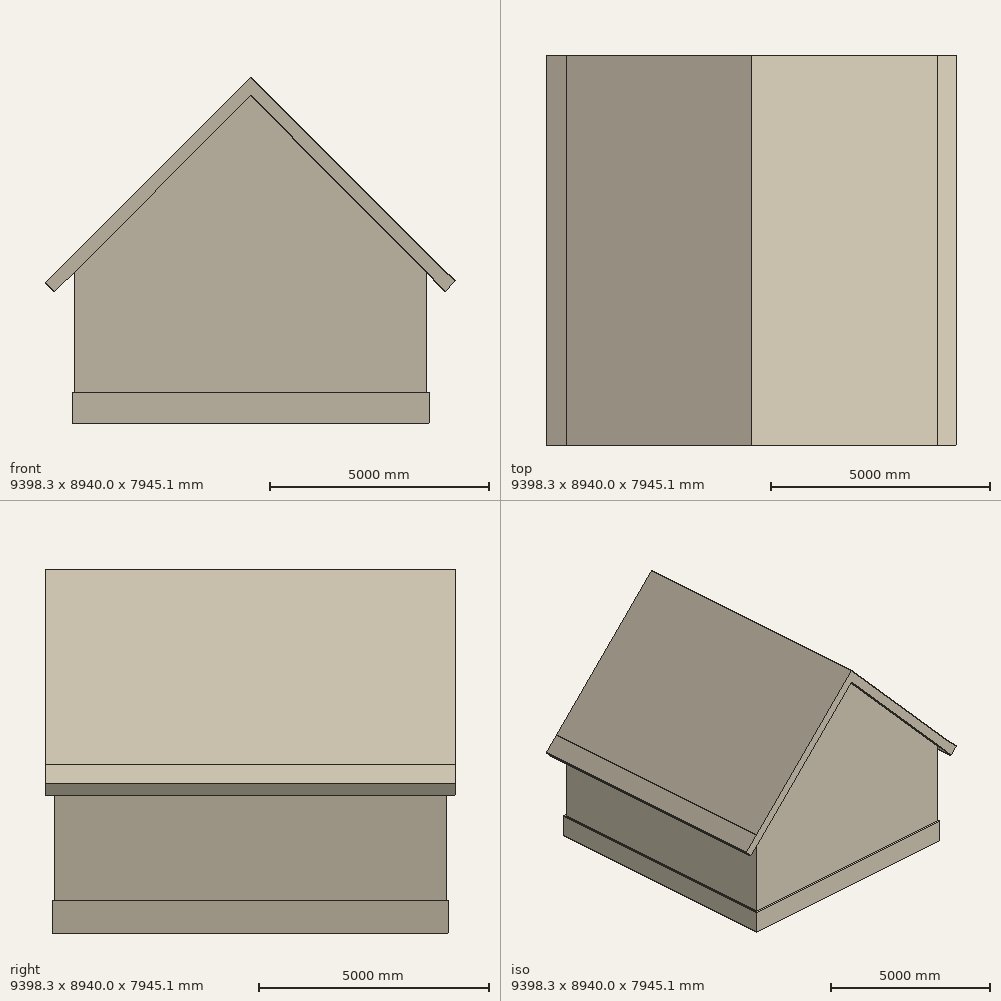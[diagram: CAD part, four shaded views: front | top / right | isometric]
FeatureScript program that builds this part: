
annotation { "Feature Type Name" : "Feature", "Feature Type Description" : "" }
export const myFeature = defineFeature(function(context is Context, id is Id, definition is map)
    precondition{}
    {
        {
            var Q0;
            Q0=qCreatedBy(makeId("Top.planeOp"),FACE);
            var sketch = newSketch(context, id + "F0", { "sketchPlane" : qUnion([Q0])});
            skLineSegment(sketch, "E0.bottom", {"start": v(0, 0) * mm, "end": v(8170, 0) * mm});
            skLineSegment(sketch, "E0.top", {"start": v(0, 8640) * mm, "end": v(8170, 8640) * mm});
            skLineSegment(sketch, "E0.left", {"start": v(0, 0) * mm, "end": v(0, 8640) * mm});
            skLineSegment(sketch, "E0.right", {"start": v(8170, 0) * mm, "end": v(8170, 8640) * mm});
            skSolve(sketch);
        }
        {
            var Q0;
            Q0 = qSketchRegion(id + "F0", true);
            extrude(context, id + "F1", {"entities" : qUnion([Q0]), "oppositeDirection" : true, "depth" : 720 * mm, "offsetDistance" : 25 * mm});
        }
        {
            var Q0;
            Q0=makeQuery(id+"F1.opExtrude","CAP_FACE",FACE,{"disambiguationData":[OSD([sQuery(id+"F0.wireOp",EDGE,"E0.bottom"),sQuery(id+"F0.wireOp",EDGE,"E0.top"),sQuery(id+"F0.wireOp",EDGE,"E0.left"),sQuery(id+"F0.wireOp",EDGE,"E0.right")])],"isStart":true});
            var sketch = newSketch(context, id + "F2", { "sketchPlane" : qUnion([Q0])});
            skLineSegment(sketch, "E1.0", {"start": v(8120, 8590) * mm, "end": v(50, 8590) * mm});
            skLineSegment(sketch, "E1.1", {"start": v(8120, 50) * mm, "end": v(8120, 8590) * mm});
            skLineSegment(sketch, "E1.2", {"start": v(50, 50) * mm, "end": v(8120, 50) * mm});
            skLineSegment(sketch, "E1.3", {"start": v(50, 8590) * mm, "end": v(50, 50) * mm});
            skSolve(sketch);
        }
        {
            var Q0;
            Q0 = qSketchRegion(id + "F2", true);
            extrude(context, id + "F3", {"entities" : qUnion([Q0]), "operationType" : NewBodyOperationType.ADD, "depth" : 2750 * mm, "offsetDistance" : 25 * mm});
        }
        {
            var Q0;
            Q0=makeQuery(id+"F3.opExtrude","SWEPT_FACE",FACE,{"disambiguationData":[OSD([sQuery(id+"F2.wireOp",EDGE,"E1.2")])]});
            var sketch = newSketch(context, id + "F4", { "sketchPlane" : qUnion([Q0])});
            skLineSegment(sketch, "E2", {"start": v(50, 2750) * mm, "end": v(4085, 6800) * mm});
            skLineSegment(sketch, "E3", {"start": v(4085, 6800) * mm, "end": v(8120, 2750) * mm});
            skLineSegment(sketch, "E4", {"start": v(8120, 2750) * mm, "end": v(50, 2750) * mm});
            skLineSegment(sketch, "E5", {"start": v(4085, 6800) * mm, "end": v(4085, 2750) * mm, "construction": true});
            skPoint(sketch, "E5.endSnap0", {"position": v(4085, 2750) * mm});
            skSolve(sketch);
        }
        {
            var Q0;
            Q0 = qSketchRegion(id + "F4", true);
            var Q1;
            Q1=makeQuery(id+"F3.opExtrude","SWEPT_FACE",FACE,{"disambiguationData":[OSD([sQuery(id+"F2.wireOp",EDGE,"E1.0")])]});
            extrude(context, id + "F5", {"entities" : qUnion([Q0]), "operationType" : NewBodyOperationType.ADD, "endBound" : BoundingType.UP_TO_SURFACE, "oppositeDirection" : true, "depth" : 25 * mm, "endBoundEntityFace" : qUnion([Q1]), "offsetDistance" : 25 * mm});
        }
        {
            var Q0;
            Q0=makeQuery(id+"F5.boolean.opBoolean","MERGE",FACE,{"derivedFrom":[makeQuery(id+"F3.opExtrude","SWEPT_FACE",FACE,{"disambiguationData":[OSD([sQuery(id+"F2.wireOp",EDGE,"E1.2")])]}),makeQuery(id+"F5.opExtrude","CAP_FACE",FACE,{"disambiguationData":[OSD([sQuery(id+"F4.wireOp",EDGE,"E2"),sQuery(id+"F4.wireOp",EDGE,"E3"),sQuery(id+"F4.wireOp",EDGE,"E4")])],"isStart":true})]});
            var sketch = newSketch(context, id + "F6", { "sketchPlane" : qUnion([Q0])});
            skLineSegment(sketch, "E6.0", {"start": v(4085, 7225.05) * mm, "end": v(8332.53, 2961.74) * mm});
            skLineSegment(sketch, "E6.1", {"start": v(-162.53, 2961.74) * mm, "end": v(4085, 7225.05) * mm});
            skLineSegment(sketch, "E7", {"start": v(-162.53, 2961.74) * mm, "end": v(-623.33, 2501.3) * mm});
            skLineSegment(sketch, "E8", {"start": v(-623.33, 2501.3) * mm, "end": v(-420.13, 2297.94) * mm});
            skLineSegment(sketch, "E9", {"start": v(-420.13, 2297.94) * mm, "end": v(50, 2750) * mm});
            skLineSegment(sketch, "E10", {"start": v(8332.53, 2961.74) * mm, "end": v(8775.01, 2553.98) * mm});
            skLineSegment(sketch, "E11", {"start": v(8775.01, 2553.98) * mm, "end": v(8539.07, 2297.94) * mm});
            skLineSegment(sketch, "E12", {"start": v(8539.07, 2297.94) * mm, "end": v(8120, 2750) * mm});
            skLineSegment(sketch, "E13", {"start": v(-420.13, 2297.94) * mm, "end": v(8539.07, 2297.94) * mm, "construction": true});
            skSolve(sketch);
        }
        {
            var Q0;
            Q0=makeQuery(id+"F6.imprint","IMPRINT",FACE,{"disambiguationData":[TD([[makeQuery(id+"F6.imprint","IMPRINT",EDGE,{"derivedFrom":sQuery(id+"F6.wireOp",EDGE,"E6.0")}),-1.0]])]});
            var Q1;
            Q1=makeQuery(id+"F5.boolean.opBoolean","MERGE",FACE,{"derivedFrom":[makeQuery(id+"F3.opExtrude","SWEPT_FACE",FACE,{"disambiguationData":[OSD([sQuery(id+"F2.wireOp",EDGE,"E1.0")])]}),makeQuery(id+"F5.opExtrude","CAP_FACE",FACE,{"disambiguationData":[OSD([sQuery(id+"F4.wireOp",EDGE,"E2"),sQuery(id+"F4.wireOp",EDGE,"E3"),sQuery(id+"F4.wireOp",EDGE,"E4")])],"isStart":false})]});
            extrude(context, id + "F7", {"entities" : qUnion([Q0]), "operationType" : NewBodyOperationType.ADD, "endBound" : BoundingType.UP_TO_SURFACE, "oppositeDirection" : true, "depth" : 25 * mm, "endBoundEntityFace" : qUnion([Q1]), "hasOffset" : true, "offsetDistance" : 200 * mm, "offsetOppositeDirection" : true, "hasSecondDirection" : true, "secondDirectionOppositeDirection" : false, "secondDirectionDepth" : 200 * mm});
        }
    });
